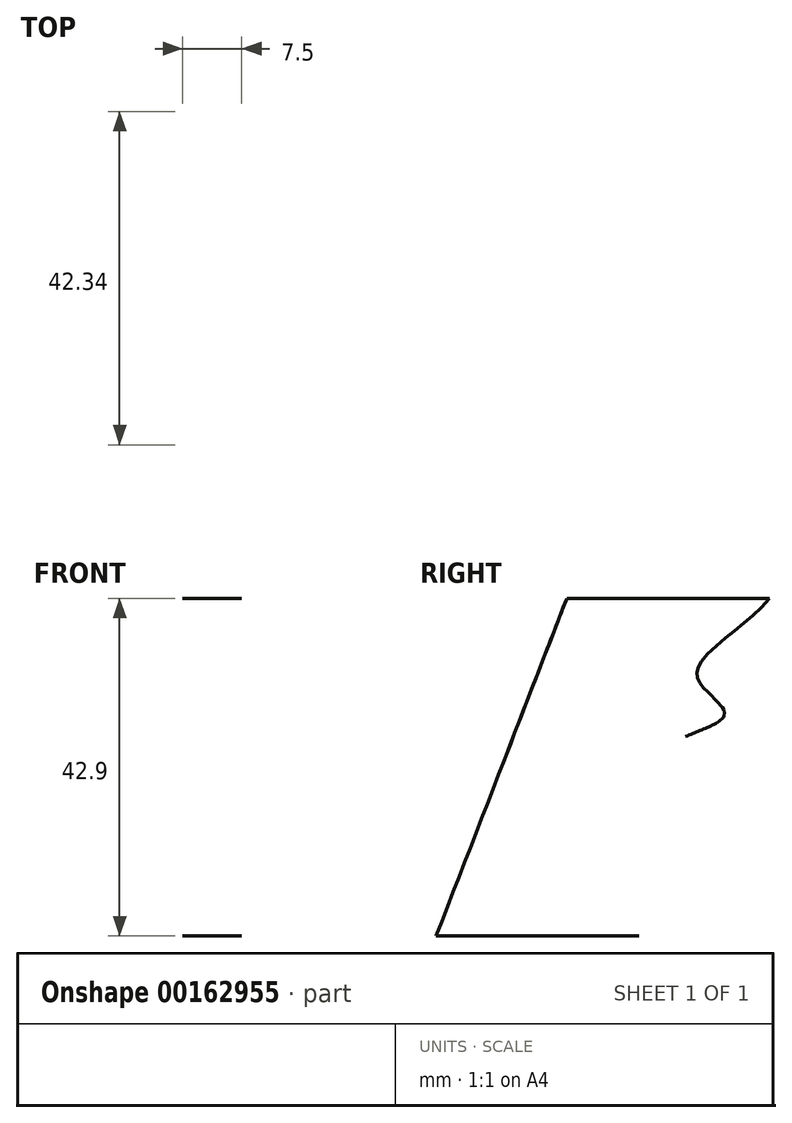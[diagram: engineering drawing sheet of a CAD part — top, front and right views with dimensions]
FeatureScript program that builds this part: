
annotation { "Feature Type Name" : "Feature", "Feature Type Description" : "" }
export const myFeature = defineFeature(function(context is Context, id is Id, definition is map)
    precondition{}
    {
        {
            var Q0;
            Q0=qCreatedBy(makeId("Right.planeOp"),FACE);
            var sketch = newSketch(context, id + "F0", { "sketchPlane" : qUnion([Q0])});
            skLineSegment(sketch, "E0", {"start": v(-19.95, 31.67) * mm, "end": v(-36.53, -11.23) * mm});
            skFitSpline(sketch, "E1", {"points": [v(5.81, 31.67) * mm, v(-3.38, 21.76) * mm, v(0.05, 16.76) * mm, v(-6.99, 12.43) * mm, v(-3.56, 7.43) * mm, v(-10.6, 3.1) * mm, v(-7.17, -1.9) * mm, v(-14.2, -6.23) * mm, v(-10.77, -11.23) * mm], "startDerivative": vector(-59.24, -72.78) * mm, "endDerivative": vector(23.43, -61.73) * mm});
            skLineSegment(sketch, "E2", {"start": v(5.81, 31.67) * mm, "end": v(-10.77, -11.23) * mm, "construction": true});
            skLineSegment(sketch, "E3", {"start": v(-19.95, 31.67) * mm, "end": v(5.81, 31.67) * mm, "construction": true});
            skLineSegment(sketch, "E4", {"start": v(-36.53, -11.23) * mm, "end": v(-10.77, -11.23) * mm, "construction": true});
            skSolve(sketch);
        }
        {
            var Q0;
            Q0=sQuery(id+"F0.wireOp",EDGE,"E3");
            cPlane(context, id + "F1", {"entities" : qUnion([Q0]), "cplaneType" : CPlaneType.LINE_ANGLE, "offset" : 25 * mm, "angle" : 0 * degree, "width" : 150 * mm, "height" : 150 * mm});
        }
        {
            var Q0;
            Q0=sQuery(id+"F0.wireOp",EDGE,"E4");
            cPlane(context, id + "F2", {"entities" : qUnion([Q0]), "cplaneType" : CPlaneType.LINE_ANGLE, "offset" : 25 * mm, "angle" : 0 * degree, "width" : 150 * mm, "height" : 150 * mm});
        }
        {
            var Q0;
            Q0=qCreatedBy(id+"F1.planeOp",FACE);
            var sketch = newSketch(context, id + "F3", { "sketchPlane" : qUnion([Q0])});
            skLineSegment(sketch, "E5.0", {"start": v(0, -19.95) * mm, "end": v(0, 5.81) * mm, "construction": true});
            skLineSegment(sketch, "E6.bottom", {"start": v(-0.25, -19.95) * mm, "end": v(0.25, -19.95) * mm});
            skLineSegment(sketch, "E6.top", {"start": v(-0.25, 5.81) * mm, "end": v(0.25, 5.81) * mm});
            skLineSegment(sketch, "E6.left", {"start": v(-3.75, -16.45) * mm, "end": v(-3.75, 2.31) * mm});
            skLineSegment(sketch, "E6.right", {"start": v(3.75, -16.45) * mm, "end": v(3.75, 2.31) * mm});
            skPoint(sketch, "E7.visualSharp", {"position": v(-3.75, -19.95) * mm});
            skArc(sketch, "E7.filletArc", {"start": v(-3.75, -16.45) * mm, "mid": v(-2.72, -18.92) * mm, "end": v(-0.25, -19.95) * mm});
            skPoint(sketch, "E8.visualSharp", {"position": v(3.75, -19.95) * mm});
            skArc(sketch, "E8.filletArc", {"start": v(0.25, -19.95) * mm, "mid": v(2.72, -18.92) * mm, "end": v(3.75, -16.45) * mm});
            skPoint(sketch, "E9.visualSharp", {"position": v(3.75, 5.81) * mm});
            skArc(sketch, "E9.filletArc", {"start": v(3.75, 2.31) * mm, "mid": v(2.72, 4.79) * mm, "end": v(0.25, 5.81) * mm});
            skPoint(sketch, "E10.visualSharp", {"position": v(-3.75, 5.81) * mm});
            skArc(sketch, "E10.filletArc", {"start": v(-0.25, 5.81) * mm, "mid": v(-2.72, 4.79) * mm, "end": v(-3.75, 2.31) * mm});
            skSolve(sketch);
        }
        {
            var Q0;
            Q0=qCreatedBy(id+"F2.planeOp",FACE);
            var sketch = newSketch(context, id + "F4", { "sketchPlane" : qUnion([Q0])});
            skLineSegment(sketch, "E11.0", {"start": v(0, -36.53) * mm, "end": v(0, -10.77) * mm, "construction": true});
            skLineSegment(sketch, "E12.bottom", {"start": v(-0.25, -36.53) * mm, "end": v(0.25, -36.53) * mm});
            skLineSegment(sketch, "E12.top", {"start": v(-0.25, -10.77) * mm, "end": v(0.25, -10.77) * mm});
            skLineSegment(sketch, "E12.left", {"start": v(-3.75, -33.03) * mm, "end": v(-3.75, -14.27) * mm});
            skLineSegment(sketch, "E12.right", {"start": v(3.75, -33.03) * mm, "end": v(3.75, -14.27) * mm});
            skPoint(sketch, "E13.visualSharp", {"position": v(-3.75, -36.53) * mm});
            skArc(sketch, "E13.filletArc", {"start": v(-3.75, -33.03) * mm, "mid": v(-2.72, -35.5) * mm, "end": v(-0.25, -36.53) * mm});
            skPoint(sketch, "E14.visualSharp", {"position": v(3.75, -36.53) * mm});
            skArc(sketch, "E14.filletArc", {"start": v(0.25, -36.53) * mm, "mid": v(2.72, -35.5) * mm, "end": v(3.75, -33.03) * mm});
            skPoint(sketch, "E15.visualSharp", {"position": v(3.75, -10.77) * mm});
            skArc(sketch, "E15.filletArc", {"start": v(3.75, -14.27) * mm, "mid": v(2.72, -11.8) * mm, "end": v(0.25, -10.77) * mm});
            skPoint(sketch, "E16.visualSharp", {"position": v(-3.75, -10.77) * mm});
            skArc(sketch, "E16.filletArc", {"start": v(-0.25, -10.77) * mm, "mid": v(-2.72, -11.8) * mm, "end": v(-3.75, -14.27) * mm});
            skSolve(sketch);
        }
        {
            var Q0;
            Q0=makeQuery(id+"F3.imprint","IMPRINT",FACE,{"disambiguationData":[TD([[makeQuery(id+"F3.imprint","IMPRINT",EDGE,{"derivedFrom":sQuery(id+"F3.wireOp",EDGE,"E6.bottom")}),1.0]])]});
            var Q1;
            Q1=makeQuery(id+"F4.imprint","IMPRINT",FACE,{"disambiguationData":[TD([[makeQuery(id+"F4.imprint","IMPRINT",EDGE,{"derivedFrom":sQuery(id+"F4.wireOp",EDGE,"E12.bottom")}),1.0]])]});
            var Q2;
            Q2=sQuery(id+"F0.wireOp",EDGE,"E0");
            var Q3;
            Q3=sQuery(id+"F0.wireOp",EDGE,"E1");
            loft(context, id + "F5", {"addGuides" : true, "sheetProfilesArray" : [{ "sheetProfileEntities" : qUnion([Q0]) }, { "sheetProfileEntities" : qUnion([Q1]) }], "guidesArray" : [{ "guideEntities" : qUnion([Q2]), "guideDerivativeType" : LoftGuideDerivativeType.DEFAULT, "guideDerivativeMagnitude" : 1 }, { "guideEntities" : qUnion([Q3]), "guideDerivativeType" : LoftGuideDerivativeType.DEFAULT, "guideDerivativeMagnitude" : 1 }]});
        }
    });
